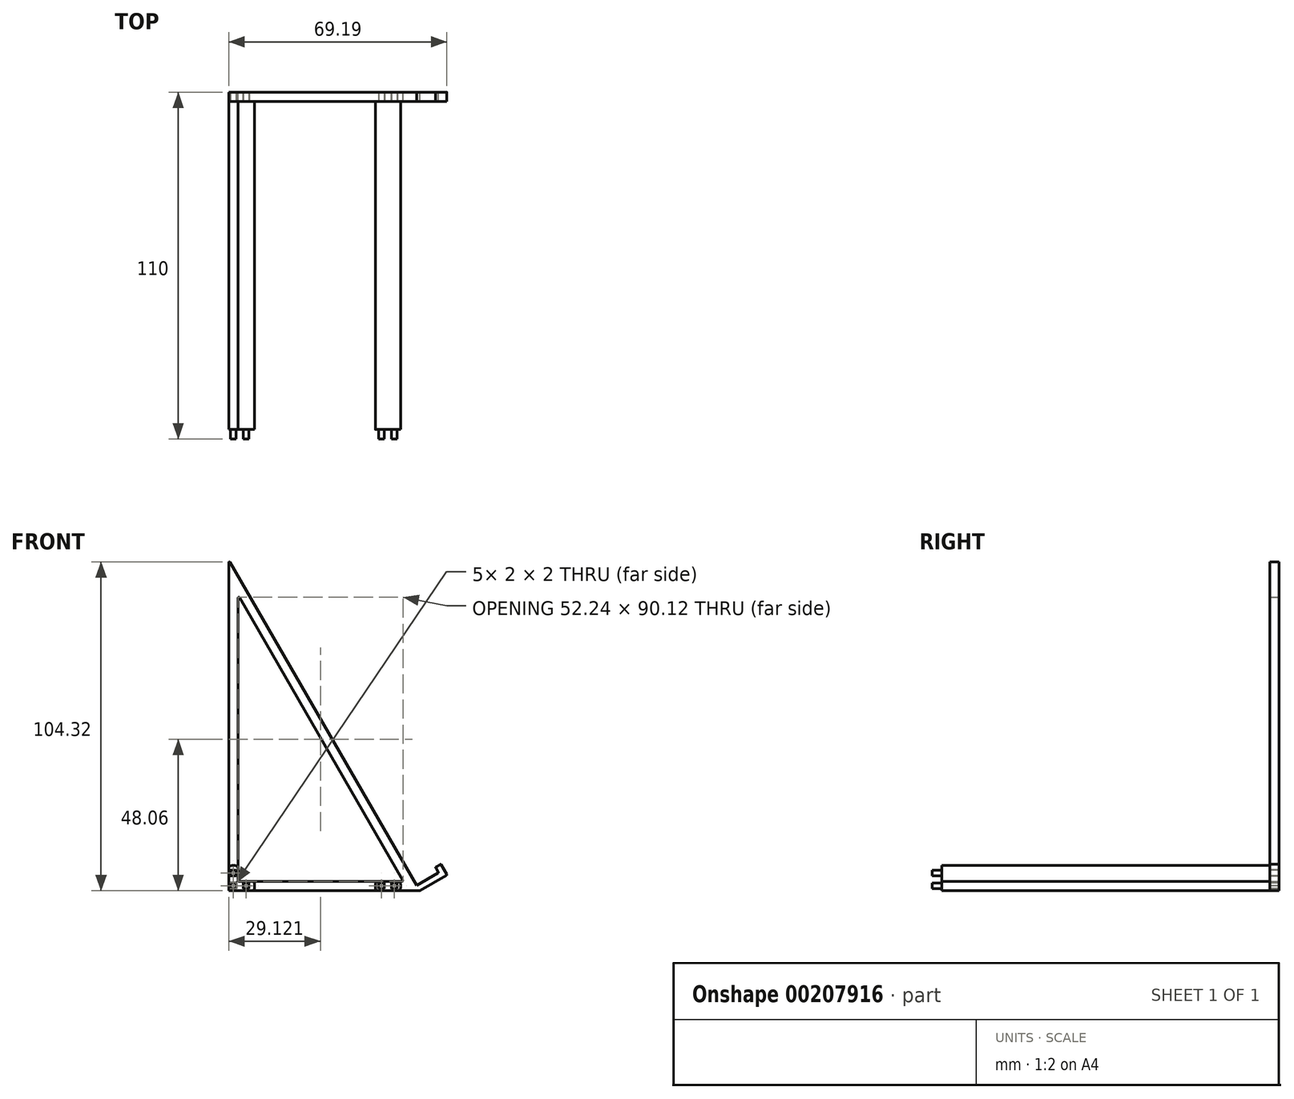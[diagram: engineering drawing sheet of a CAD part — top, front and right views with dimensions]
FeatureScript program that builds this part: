
annotation { "Feature Type Name" : "Feature", "Feature Type Description" : "" }
export const myFeature = defineFeature(function(context is Context, id is Id, definition is map)
    precondition{}
    {
        {
            var Q0;
            Q0=qCreatedBy(makeId("Front.planeOp"),FACE);
            var sketch = newSketch(context, id + "F0", { "sketchPlane" : qUnion([Q0])});
            skLineSegment(sketch, "E0", {"start": v(0, 0) * mm, "end": v(0, 104.07) * mm});
            skLineSegment(sketch, "E1", {"start": v(0.47, 104.2) * mm, "end": v(60.62, 0) * mm});
            skLineSegment(sketch, "E2", {"start": v(60.62, 0) * mm, "end": v(0, 0) * mm});
            skLineSegment(sketch, "E3", {"start": v(60.62, 0) * mm, "end": v(69.07, 4.88) * mm});
            skLineSegment(sketch, "E4", {"start": v(69.16, 5.22) * mm, "end": v(67.4, 8.25) * mm});
            skLineSegment(sketch, "E5.0", {"start": v(66.42, 5.95) * mm, "end": v(65.67, 7.25) * mm});
            skLineSegment(sketch, "E5.1", {"start": v(59.62, 1.73) * mm, "end": v(66.33, 5.6) * mm});
            skLineSegment(sketch, "E6", {"start": v(67.07, 8.34) * mm, "end": v(65.77, 7.59) * mm});
            skLineSegment(sketch, "E7.0", {"start": v(3.47, 93) * mm, "end": v(55.2, 3.37) * mm});
            skLineSegment(sketch, "E7.1", {"start": v(3, 3.25) * mm, "end": v(3, 92.87) * mm});
            skLineSegment(sketch, "E7.2", {"start": v(55, 3) * mm, "end": v(3.25, 3) * mm});
            skPoint(sketch, "E8.visualSharp", {"position": v(3, 93.8) * mm});
            skArc(sketch, "E8.filletArc", {"start": v(3.47, 93) * mm, "mid": v(3.19, 93.11) * mm, "end": v(3, 92.87) * mm});
            skPoint(sketch, "E9.visualSharp", {"position": v(0, 105) * mm});
            skArc(sketch, "E9.filletArc", {"start": v(0.47, 104.2) * mm, "mid": v(0.19, 104.3) * mm, "end": v(0, 104.07) * mm});
            skPoint(sketch, "E10.visualSharp", {"position": v(55.43, 3) * mm});
            skArc(sketch, "E10.filletArc", {"start": v(55, 3) * mm, "mid": v(55.2, 3.12) * mm, "end": v(55.2, 3.37) * mm});
            skPoint(sketch, "E11.visualSharp", {"position": v(3, 3) * mm});
            skArc(sketch, "E11.filletArc", {"start": v(3, 3.25) * mm, "mid": v(3.07, 3.07) * mm, "end": v(3.25, 3) * mm});
            skPoint(sketch, "E12.visualSharp", {"position": v(66.55, 5.73) * mm});
            skArc(sketch, "E12.filletArc", {"start": v(66.33, 5.6) * mm, "mid": v(66.45, 5.76) * mm, "end": v(66.42, 5.95) * mm});
            skPoint(sketch, "E13.visualSharp", {"position": v(65.55, 7.46) * mm});
            skArc(sketch, "E13.filletArc", {"start": v(65.77, 7.59) * mm, "mid": v(65.65, 7.44) * mm, "end": v(65.67, 7.25) * mm});
            skPoint(sketch, "E14.visualSharp", {"position": v(67.28, 8.46) * mm});
            skArc(sketch, "E14.filletArc", {"start": v(67.4, 8.25) * mm, "mid": v(67.26, 8.36) * mm, "end": v(67.07, 8.34) * mm});
            skPoint(sketch, "E15.visualSharp", {"position": v(69.28, 5) * mm});
            skArc(sketch, "E15.filletArc", {"start": v(69.07, 4.88) * mm, "mid": v(69.18, 5.03) * mm, "end": v(69.16, 5.22) * mm});
            skSolve(sketch);
        }
        {
            var Q0;
            Q0 = qSketchRegion(id + "F0", true);
            extrude(context, id + "F1", {"entities" : qUnion([Q0]), "depth" : 3 * mm});
        }
        {
            var Q0;
            Q0=makeQuery(id+"F1.opExtrude","CAP_FACE",FACE,{"disambiguationData":[OSD([sQuery(id+"F0.wireOp",EDGE,"E0"),sQuery(id+"F0.wireOp",EDGE,"E1"),sQuery(id+"F0.wireOp",EDGE,"E2"),sQuery(id+"F0.wireOp",EDGE,"E3"),sQuery(id+"F0.wireOp",EDGE,"E4"),sQuery(id+"F0.wireOp",EDGE,"E5.0"),sQuery(id+"F0.wireOp",EDGE,"E5.1"),sQuery(id+"F0.wireOp",EDGE,"E6"),sQuery(id+"F0.wireOp",EDGE,"E7.0"),sQuery(id+"F0.wireOp",EDGE,"E7.1"),sQuery(id+"F0.wireOp",EDGE,"E7.2")])],"isStart":false});
            var sketch = newSketch(context, id + "F2", { "sketchPlane" : qUnion([Q0])});
            skLineSegment(sketch, "E16", {"start": v(3, 0) * mm, "end": v(3, 3.25) * mm, "construction": true});
            skLineSegment(sketch, "E17", {"start": v(3, 1.62) * mm, "end": v(0, 1.62) * mm, "construction": true});
            skLineSegment(sketch, "E18.bottom", {"start": v(0.5, 2.62) * mm, "end": v(2.5, 2.62) * mm});
            skLineSegment(sketch, "E18.top", {"start": v(0.5, 0.62) * mm, "end": v(2.5, 0.62) * mm});
            skLineSegment(sketch, "E18.left", {"start": v(0.5, 2.62) * mm, "end": v(0.5, 0.62) * mm});
            skLineSegment(sketch, "E18.right", {"start": v(2.5, 2.62) * mm, "end": v(2.5, 0.62) * mm});
            skPoint(sketch, "E18.middle", {"position": v(1.5, 1.62) * mm});
            skLineSegment(sketch, "E19.bottom", {"start": v(0.5, 4.62) * mm, "end": v(2.5, 4.62) * mm});
            skLineSegment(sketch, "E19.top", {"start": v(0.5, 6.62) * mm, "end": v(2.5, 6.62) * mm});
            skLineSegment(sketch, "E19.left", {"start": v(0.5, 4.62) * mm, "end": v(0.5, 6.62) * mm});
            skLineSegment(sketch, "E19.right", {"start": v(2.5, 4.62) * mm, "end": v(2.5, 6.62) * mm});
            skPoint(sketch, "E19.middle", {"position": v(1.5, 5.62) * mm});
            skPoint(sketch, "E19.middle.positionSnap0", {"position": v(1.5, 2.62) * mm});
            skPoint(sketch, "E19.centerSnap0", {"position": v(1.5, 2.62) * mm});
            skLineSegment(sketch, "E20.bottom", {"start": v(4.5, 0.62) * mm, "end": v(6.5, 0.62) * mm});
            skLineSegment(sketch, "E20.top", {"start": v(4.5, 2.62) * mm, "end": v(6.5, 2.62) * mm});
            skLineSegment(sketch, "E20.left", {"start": v(4.5, 0.62) * mm, "end": v(4.5, 2.62) * mm});
            skLineSegment(sketch, "E20.right", {"start": v(6.5, 0.62) * mm, "end": v(6.5, 2.62) * mm});
            skPoint(sketch, "E20.middle", {"position": v(5.5, 1.62) * mm});
            skLineSegment(sketch, "E21.bottom", {"start": v(51.5, 0.62) * mm, "end": v(53.5, 0.62) * mm});
            skLineSegment(sketch, "E21.top", {"start": v(51.5, 2.62) * mm, "end": v(53.5, 2.62) * mm});
            skLineSegment(sketch, "E21.left", {"start": v(51.5, 0.62) * mm, "end": v(51.5, 2.62) * mm});
            skLineSegment(sketch, "E21.right", {"start": v(53.5, 0.62) * mm, "end": v(53.5, 2.62) * mm});
            skPoint(sketch, "E21.middle", {"position": v(52.5, 1.62) * mm});
            skPoint(sketch, "E21.middle.positionSnap0", {"position": v(6.5, 1.62) * mm});
            skPoint(sketch, "E21.centerSnap0", {"position": v(6.5, 1.62) * mm});
            skLineSegment(sketch, "E22.1.0.0", {"start": v(47.5, 0.62) * mm, "end": v(47.5, 2.62) * mm});
            skLineSegment(sketch, "E22.1.0.1", {"start": v(47.5, 2.62) * mm, "end": v(49.5, 2.62) * mm});
            skLineSegment(sketch, "E22.1.0.2", {"start": v(49.5, 0.62) * mm, "end": v(49.5, 2.62) * mm});
            skLineSegment(sketch, "E22.1.0.3", {"start": v(47.5, 0.62) * mm, "end": v(49.5, 0.62) * mm});
            skLineSegment(sketch, "E22.direction1", {"start": v(51.5, 0.62) * mm, "end": v(47.5, 0.62) * mm, "construction": true});
            skLineSegment(sketch, "E23.0", {"start": v(51.6, 2.52) * mm, "end": v(53.4, 2.52) * mm});
            skLineSegment(sketch, "E23.1", {"start": v(51.6, 0.72) * mm, "end": v(51.6, 2.52) * mm});
            skLineSegment(sketch, "E23.2", {"start": v(51.6, 0.72) * mm, "end": v(53.4, 0.72) * mm});
            skLineSegment(sketch, "E23.3", {"start": v(53.4, 0.72) * mm, "end": v(53.4, 2.52) * mm});
            skLineSegment(sketch, "E24.0", {"start": v(47.6, 2.52) * mm, "end": v(49.4, 2.52) * mm});
            skLineSegment(sketch, "E24.1", {"start": v(47.6, 0.72) * mm, "end": v(47.6, 2.52) * mm});
            skLineSegment(sketch, "E24.2", {"start": v(47.6, 0.72) * mm, "end": v(49.4, 0.72) * mm});
            skLineSegment(sketch, "E24.3", {"start": v(49.4, 0.72) * mm, "end": v(49.4, 2.52) * mm});
            skLineSegment(sketch, "E25.0", {"start": v(4.6, 0.72) * mm, "end": v(6.4, 0.72) * mm});
            skLineSegment(sketch, "E25.1", {"start": v(4.6, 0.72) * mm, "end": v(4.6, 2.52) * mm});
            skLineSegment(sketch, "E25.2", {"start": v(4.6, 2.52) * mm, "end": v(6.4, 2.52) * mm});
            skLineSegment(sketch, "E25.3", {"start": v(6.4, 0.72) * mm, "end": v(6.4, 2.52) * mm});
            skLineSegment(sketch, "E26.0", {"start": v(2.4, 2.52) * mm, "end": v(2.4, 0.72) * mm});
            skLineSegment(sketch, "E26.1", {"start": v(0.6, 2.52) * mm, "end": v(2.4, 2.52) * mm});
            skLineSegment(sketch, "E26.2", {"start": v(0.6, 2.52) * mm, "end": v(0.6, 0.72) * mm});
            skLineSegment(sketch, "E26.3", {"start": v(0.6, 0.72) * mm, "end": v(2.4, 0.72) * mm});
            skLineSegment(sketch, "E27.0", {"start": v(0.6, 4.72) * mm, "end": v(2.4, 4.72) * mm});
            skLineSegment(sketch, "E27.1", {"start": v(0.6, 4.72) * mm, "end": v(0.6, 6.52) * mm});
            skLineSegment(sketch, "E27.2", {"start": v(0.6, 6.52) * mm, "end": v(2.4, 6.52) * mm});
            skLineSegment(sketch, "E27.3", {"start": v(2.4, 4.72) * mm, "end": v(2.4, 6.52) * mm});
            skSolve(sketch);
        }
        {
            var Q0;
            Q0 = qSketchRegion(id + "F2", true);
            var Q1;
            Q1=makeQuery(id+"F2.imprint","IMPRINT",FACE,{"disambiguationData":[TD([[makeQuery(id+"F2.imprint","IMPRINT",EDGE,{"derivedFrom":sQuery(id+"F2.wireOp",EDGE,"E27.0")}),1.0]])]});
            var Q2;
            Q2=makeQuery(id+"F2.imprint","IMPRINT",FACE,{"disambiguationData":[TD([[makeQuery(id+"F2.imprint","IMPRINT",EDGE,{"derivedFrom":sQuery(id+"F2.wireOp",EDGE,"E26.0")}),-1.0]])]});
            var Q3;
            Q3=makeQuery(id+"F2.imprint","IMPRINT",FACE,{"disambiguationData":[TD([[makeQuery(id+"F2.imprint","IMPRINT",EDGE,{"derivedFrom":sQuery(id+"F2.wireOp",EDGE,"E25.0")}),1.0]])]});
            var Q4;
            Q4=makeQuery(id+"F2.imprint","IMPRINT",FACE,{"disambiguationData":[TD([[makeQuery(id+"F2.imprint","IMPRINT",EDGE,{"derivedFrom":sQuery(id+"F2.wireOp",EDGE,"E24.0")}),-1.0]])]});
            var Q5;
            Q5=makeQuery(id+"F2.imprint","IMPRINT",FACE,{"disambiguationData":[TD([[makeQuery(id+"F2.imprint","IMPRINT",EDGE,{"derivedFrom":sQuery(id+"F2.wireOp",EDGE,"E23.0")}),-1.0]])]});
            var Q6;
            Q6=makeQuery(id+"F1.opExtrude","CAP_FACE",FACE,{"disambiguationData":[OSD([sQuery(id+"F0.wireOp",EDGE,"E0"),sQuery(id+"F0.wireOp",EDGE,"E1"),sQuery(id+"F0.wireOp",EDGE,"E2"),sQuery(id+"F0.wireOp",EDGE,"E3"),sQuery(id+"F0.wireOp",EDGE,"E4"),sQuery(id+"F0.wireOp",EDGE,"E5.0"),sQuery(id+"F0.wireOp",EDGE,"E5.1"),sQuery(id+"F0.wireOp",EDGE,"E6"),sQuery(id+"F0.wireOp",EDGE,"E7.0"),sQuery(id+"F0.wireOp",EDGE,"E7.1"),sQuery(id+"F0.wireOp",EDGE,"E7.2")])],"isStart":true});
            extrude(context, id + "F3", {"entities" : qUnion([Q0, Q1, Q2, Q3, Q4, Q5]), "operationType" : NewBodyOperationType.REMOVE, "endBound" : BoundingType.UP_TO_SURFACE, "oppositeDirection" : true, "endBoundEntityFace" : qUnion([Q6]), "depth" : 25 * mm});
        }
        {
            var Q0;
            Q0=makeQuery(id+"F1.opExtrude","CAP_FACE",FACE,{"disambiguationData":[OSD([sQuery(id+"F0.wireOp",EDGE,"E0"),sQuery(id+"F0.wireOp",EDGE,"E1"),sQuery(id+"F0.wireOp",EDGE,"E2"),sQuery(id+"F0.wireOp",EDGE,"E3"),sQuery(id+"F0.wireOp",EDGE,"E4"),sQuery(id+"F0.wireOp",EDGE,"E5.0"),sQuery(id+"F0.wireOp",EDGE,"E5.1"),sQuery(id+"F0.wireOp",EDGE,"E6"),sQuery(id+"F0.wireOp",EDGE,"E7.0"),sQuery(id+"F0.wireOp",EDGE,"E7.1"),sQuery(id+"F0.wireOp",EDGE,"E7.2")])],"isStart":false});
            var sketch = newSketch(context, id + "F4", { "sketchPlane" : qUnion([Q0])});
            skLineSegment(sketch, "E28.bottom", {"start": v(1, 8) * mm, "end": v(2, 8) * mm});
            skLineSegment(sketch, "E28.top", {"start": v(1, 0) * mm, "end": v(3, 0) * mm});
            skLineSegment(sketch, "E28.left", {"start": v(0, 7) * mm, "end": v(0, 1) * mm});
            skLineSegment(sketch, "E28.right", {"start": v(3, 7) * mm, "end": v(3, 0) * mm});
            skLineSegment(sketch, "E29.bottom", {"start": v(3.25, 3) * mm, "end": v(7.25, 3) * mm});
            skLineSegment(sketch, "E29.top", {"start": v(3.25, 0) * mm, "end": v(7.25, 0) * mm});
            skLineSegment(sketch, "E29.left", {"start": v(3.25, 3) * mm, "end": v(3.25, 0) * mm});
            skLineSegment(sketch, "E29.right", {"start": v(8.25, 2) * mm, "end": v(8.25, 1) * mm});
            skLineSegment(sketch, "E30.bottom", {"start": v(47.5, 3) * mm, "end": v(53.5, 3) * mm});
            skLineSegment(sketch, "E30.top", {"start": v(47.5, 0) * mm, "end": v(53.5, 0) * mm});
            skLineSegment(sketch, "E30.left", {"start": v(46.5, 2) * mm, "end": v(46.5, 1) * mm});
            skLineSegment(sketch, "E30.right", {"start": v(54.5, 2) * mm, "end": v(54.5, 1) * mm});
            skPoint(sketch, "E31.visualSharp", {"position": v(8.25, 0) * mm});
            skArc(sketch, "E31.filletArc", {"start": v(7.25, 0) * mm, "mid": v(7.96, 0.3) * mm, "end": v(8.25, 1) * mm});
            skPoint(sketch, "E32.visualSharp", {"position": v(8.25, 3) * mm});
            skArc(sketch, "E32.filletArc", {"start": v(8.25, 2) * mm, "mid": v(7.96, 2.7) * mm, "end": v(7.25, 3) * mm});
            skPoint(sketch, "E33.visualSharp", {"position": v(0, 8) * mm});
            skArc(sketch, "E33.filletArc", {"start": v(1, 8) * mm, "mid": v(0.3, 7.7) * mm, "end": v(0, 7) * mm});
            skPoint(sketch, "E34.visualSharp", {"position": v(3, 8) * mm});
            skArc(sketch, "E34.filletArc", {"start": v(3, 7) * mm, "mid": v(2.7, 7.7) * mm, "end": v(2, 8) * mm});
            skPoint(sketch, "E35.visualSharp", {"position": v(0, 0) * mm});
            skArc(sketch, "E35.filletArc", {"start": v(0, 1) * mm, "mid": v(0.3, 0.3) * mm, "end": v(1, 0) * mm});
            skPoint(sketch, "E36.visualSharp", {"position": v(46.5, 3) * mm});
            skArc(sketch, "E36.filletArc", {"start": v(47.5, 3) * mm, "mid": v(46.8, 2.7) * mm, "end": v(46.5, 2) * mm});
            skPoint(sketch, "E37.visualSharp", {"position": v(46.5, 0) * mm});
            skArc(sketch, "E37.filletArc", {"start": v(46.5, 1) * mm, "mid": v(46.8, 0.3) * mm, "end": v(47.5, 0) * mm});
            skPoint(sketch, "E38.visualSharp", {"position": v(54.5, 3) * mm});
            skArc(sketch, "E38.filletArc", {"start": v(54.5, 2) * mm, "mid": v(54.2, 2.7) * mm, "end": v(53.5, 3) * mm});
            skPoint(sketch, "E39.visualSharp", {"position": v(54.5, 0) * mm});
            skArc(sketch, "E39.filletArc", {"start": v(53.5, 0) * mm, "mid": v(54.2, 0.3) * mm, "end": v(54.5, 1) * mm});
            skLineSegment(sketch, "E40", {"start": v(3, 0) * mm, "end": v(3.25, 0) * mm});
            skArc(sketch, "E41", {"start": v(3, 3.25) * mm, "mid": v(3.07, 3.07) * mm, "end": v(3.25, 3) * mm});
            skSolve(sketch);
        }
        {
            var Q0;
            Q0 = qSketchRegion(id + "F4", true);
            extrude(context, id + "F5", {"entities" : qUnion([Q0]), "depth" : 104 * mm});
        }
        {
            var Q0;
            Q0=makeQuery(id+"F2.imprint","IMPRINT",FACE,{"disambiguationData":[TD([[makeQuery(id+"F2.imprint","IMPRINT",EDGE,{"derivedFrom":sQuery(id+"F2.wireOp",EDGE,"E27.0")}),1.0]])]});
            var Q1;
            Q1=makeQuery(id+"F2.imprint","IMPRINT",FACE,{"disambiguationData":[TD([[makeQuery(id+"F2.imprint","IMPRINT",EDGE,{"derivedFrom":sQuery(id+"F2.wireOp",EDGE,"E26.0")}),-1.0]])]});
            var Q2;
            Q2=makeQuery(id+"F2.imprint","IMPRINT",FACE,{"disambiguationData":[TD([[makeQuery(id+"F2.imprint","IMPRINT",EDGE,{"derivedFrom":sQuery(id+"F2.wireOp",EDGE,"E25.0")}),1.0]])]});
            extrude(context, id + "F6", {"entities" : qUnion([Q0, Q1, Q2]), "operationType" : NewBodyOperationType.ADD, "oppositeDirection" : true, "depth" : 3 * mm});
        }
        {
            var Q0;
            Q0=makeQuery(id+"F2.imprint","IMPRINT",FACE,{"disambiguationData":[TD([[makeQuery(id+"F2.imprint","IMPRINT",EDGE,{"derivedFrom":sQuery(id+"F2.wireOp",EDGE,"E23.0")}),-1.0]])]});
            var Q1;
            Q1=makeQuery(id+"F2.imprint","IMPRINT",FACE,{"disambiguationData":[TD([[makeQuery(id+"F2.imprint","IMPRINT",EDGE,{"derivedFrom":sQuery(id+"F2.wireOp",EDGE,"E24.0")}),-1.0]])]});
            extrude(context, id + "F7", {"entities" : qUnion([Q0, Q1]), "operationType" : NewBodyOperationType.ADD, "oppositeDirection" : true, "depth" : 3 * mm});
        }
        {
            var Q0;
            Q0=makeQuery(id+"F6.opExtrude","CAP_FACE",FACE,{"disambiguationData":[OSD([sQuery(id+"F2.wireOp",EDGE,"E25.0"),sQuery(id+"F2.wireOp",EDGE,"E25.1"),sQuery(id+"F2.wireOp",EDGE,"E25.2"),sQuery(id+"F2.wireOp",EDGE,"E25.3")])],"isStart":false});
            var Q1;
            Q1=makeQuery(id+"F6.opExtrude","CAP_FACE",FACE,{"disambiguationData":[OSD([sQuery(id+"F2.wireOp",EDGE,"E26.0"),sQuery(id+"F2.wireOp",EDGE,"E26.1"),sQuery(id+"F2.wireOp",EDGE,"E26.2"),sQuery(id+"F2.wireOp",EDGE,"E26.3")])],"isStart":false});
            var Q2;
            Q2=makeQuery(id+"F6.opExtrude","CAP_FACE",FACE,{"disambiguationData":[OSD([sQuery(id+"F2.wireOp",EDGE,"E27.0"),sQuery(id+"F2.wireOp",EDGE,"E27.1"),sQuery(id+"F2.wireOp",EDGE,"E27.2"),sQuery(id+"F2.wireOp",EDGE,"E27.3")])],"isStart":false});
            extrude(context, id + "F8", {"entities" : qUnion([Q0, Q1, Q2]), "operationType" : NewBodyOperationType.ADD, "oppositeDirection" : true, "depth" : 110 * mm});
        }
        {
            var Q0;
            Q0=makeQuery(id+"F7.opExtrude","CAP_FACE",FACE,{"disambiguationData":[OSD([sQuery(id+"F2.wireOp",EDGE,"E23.0"),sQuery(id+"F2.wireOp",EDGE,"E23.1"),sQuery(id+"F2.wireOp",EDGE,"E23.2"),sQuery(id+"F2.wireOp",EDGE,"E23.3")])],"isStart":false});
            var Q1;
            Q1=makeQuery(id+"F7.opExtrude","CAP_FACE",FACE,{"disambiguationData":[OSD([sQuery(id+"F2.wireOp",EDGE,"E24.0"),sQuery(id+"F2.wireOp",EDGE,"E24.1"),sQuery(id+"F2.wireOp",EDGE,"E24.2"),sQuery(id+"F2.wireOp",EDGE,"E24.3")])],"isStart":false});
            extrude(context, id + "F9", {"entities" : qUnion([Q0, Q1]), "operationType" : NewBodyOperationType.ADD, "oppositeDirection" : true, "depth" : 110 * mm});
        }
    });
